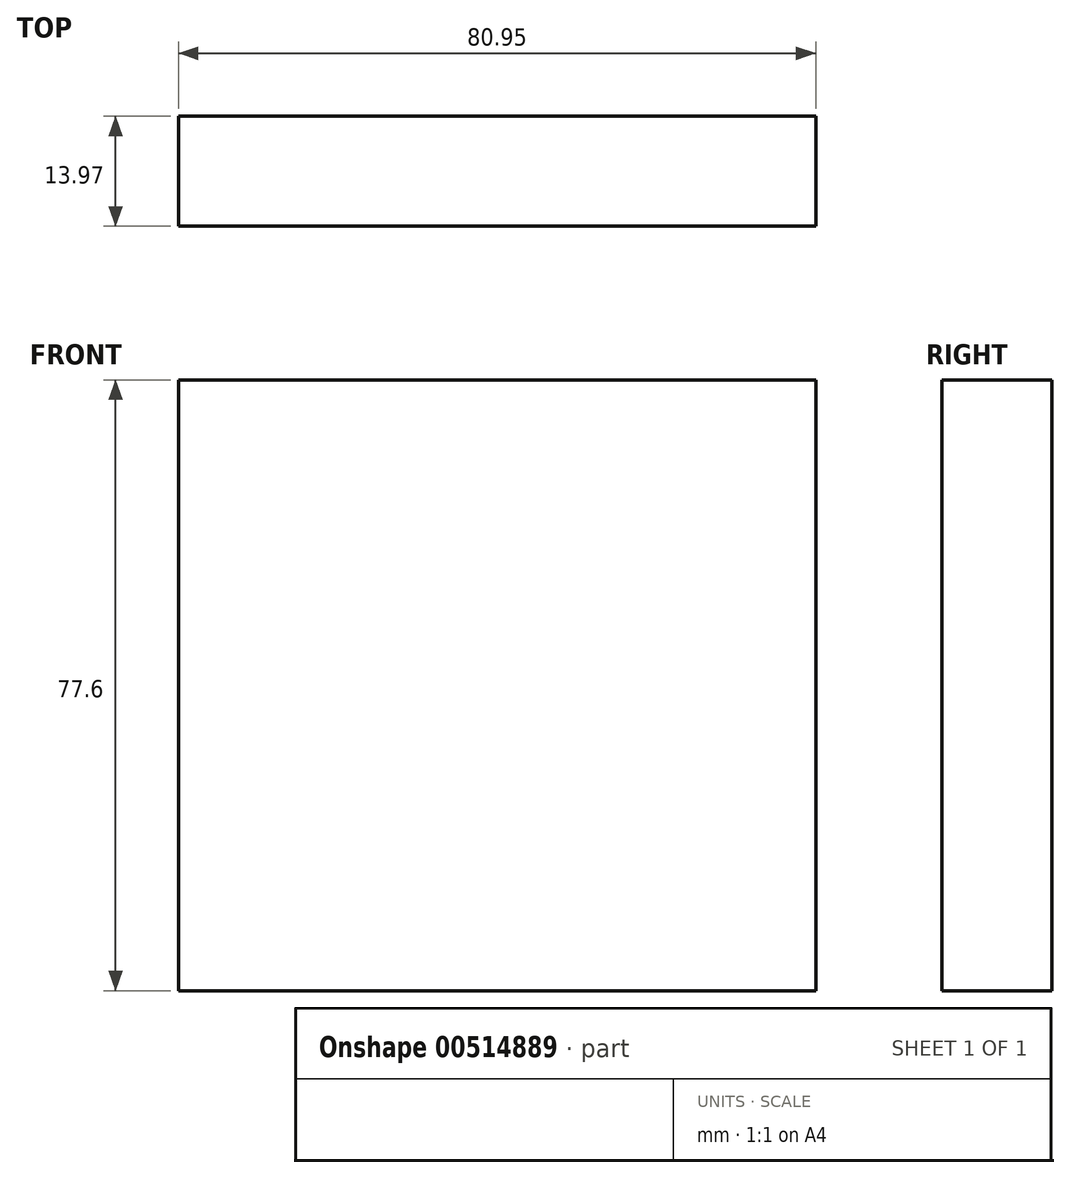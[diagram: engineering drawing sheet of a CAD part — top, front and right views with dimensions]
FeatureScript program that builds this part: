
annotation { "Feature Type Name" : "Feature", "Feature Type Description" : "" }
export const myFeature = defineFeature(function(context is Context, id is Id, definition is map)
    precondition{}
    {
        {
            var Q0;
            Q0=qCreatedBy(makeId("Front.planeOp"),FACE);
            var sketch = newSketch(context, id + "F0", { "sketchPlane" : qUnion([Q0])});
            skLineSegment(sketch, "E0.bottom", {"start": v(-43, 33.24) * mm, "end": v(37.96, 33.24) * mm});
            skLineSegment(sketch, "E0.top", {"start": v(-43, -44.36) * mm, "end": v(37.96, -44.36) * mm});
            skLineSegment(sketch, "E0.left", {"start": v(-43, 33.24) * mm, "end": v(-43, -44.36) * mm});
            skLineSegment(sketch, "E0.right", {"start": v(37.96, 33.24) * mm, "end": v(37.96, -44.36) * mm});
            skSolve(sketch);
        }
        {
            var Q0;
            Q0=makeQuery(id+"F0.imprint","IMPRINT",FACE,{"disambiguationData":[TD([[makeQuery(id+"F0.imprint","IMPRINT",EDGE,{"derivedFrom":sQuery(id+"F0.wireOp",EDGE,"E0.bottom")}),-1.0]])]});
            extrude(context, id + "F1", {"entities" : qUnion([Q0]), "depth" : 13.97 * mm, "offsetDistance" : 25.4 * mm});
        }
    });
